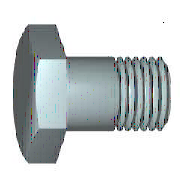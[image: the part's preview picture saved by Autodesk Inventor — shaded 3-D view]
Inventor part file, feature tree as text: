
AUTODESK INVENTOR PART (.ipt)
format: ipt  version: 2024 (Build 280153000, 153)  size: 198,656 bytes
history: native  units: mm (DEFAULTED — no unit token found)
features: extrude x1, chamfer x1, plane x1
ambient origin geometry x7: Origin, YZ Plane, XZ Plane, X Axis, Y Axis, Z Axis, Center Point
bodies: Solid1 (feature_tree), Body (feature_tree)
feature tree (3):
  extrude  "Head"  Depth=30.0mm
  chamfer  "Chamfer1"  Distance=26.0mm
  plane  "Work Plane1"
